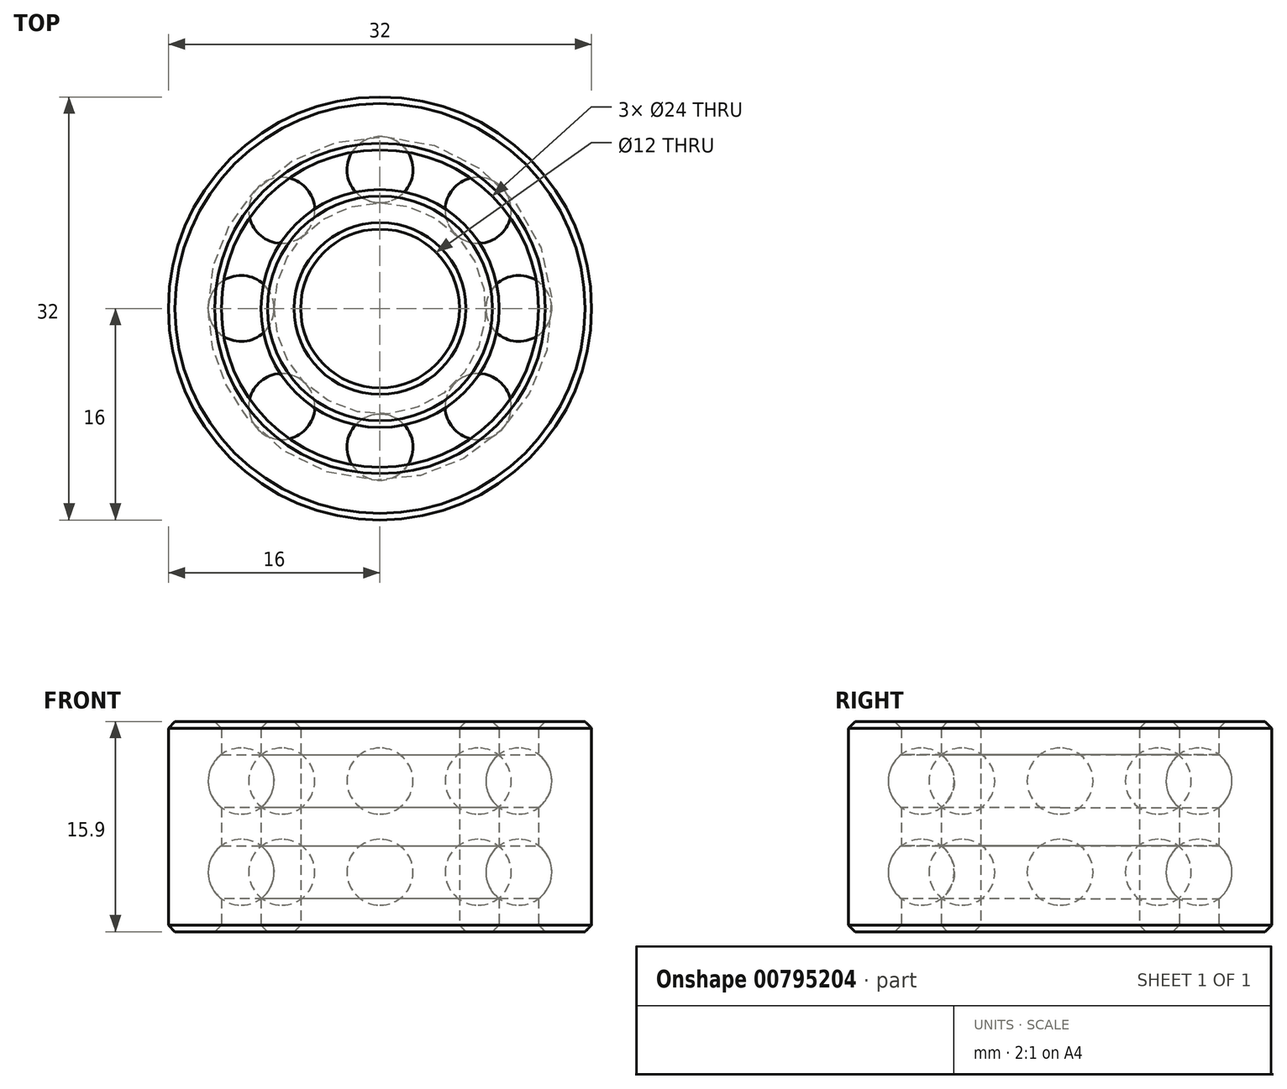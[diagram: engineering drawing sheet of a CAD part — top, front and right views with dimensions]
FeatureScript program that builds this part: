
annotation { "Feature Type Name" : "Feature", "Feature Type Description" : "" }
export const myFeature = defineFeature(function(context is Context, id is Id, definition is map)
    precondition{}
    {
        {
            var Q0;
            Q0=qCreatedBy(makeId("Top.planeOp"),FACE);
            var sketch = newSketch(context, id + "F0", { "sketchPlane" : qUnion([Q0])});
            skCircle(sketch, "E0", {"center": v(0, 0) * mm, "radius": 6 * mm});
            skCircle(sketch, "E1", {"center": v(0, 0) * mm, "radius": 16 * mm});
            skCircle(sketch, "E2", {"center": v(0, 0) * mm, "radius": 9 * mm});
            skCircle(sketch, "E3", {"center": v(0, 0) * mm, "radius": 12 * mm});
            skSolve(sketch);
        }
        {
            var Q0;
            Q0=makeQuery(id+"F0.imprint","IMPRINT",FACE,{"disambiguationData":[TD([[makeQuery(id+"F0.imprint","IMPRINT",EDGE,{"derivedFrom":sQuery(id+"F0.wireOp",EDGE,"E0")}),-1.0]])]});
            var Q1;
            Q1=makeQuery(id+"F0.imprint","IMPRINT",FACE,{"disambiguationData":[TD([[makeQuery(id+"F0.imprint","IMPRINT",EDGE,{"derivedFrom":sQuery(id+"F0.wireOp",EDGE,"E1")}),1.0]])]});
            extrude(context, id + "F1", {"entities" : qUnion([Q0, Q1]), "depth" : 15.9 * mm, "offsetDistance" : 25 * mm});
        }
        {
            var Q0;
            Q0=makeQuery(id+"F1.opExtrude","CAP_FACE",FACE,{"disambiguationData":[OSD([sQuery(id+"F0.wireOp",EDGE,"E1"),sQuery(id+"F0.wireOp",EDGE,"E3")])],"isStart":false});
            var Q1;
            Q1=makeQuery(id+"F1.opExtrude","CAP_FACE",FACE,{"disambiguationData":[OSD([sQuery(id+"F0.wireOp",EDGE,"E0"),sQuery(id+"F0.wireOp",EDGE,"E2")])],"isStart":false});
            var Q2;
            Q2=makeQuery(id+"F1.opExtrude","CAP_FACE",FACE,{"disambiguationData":[OSD([sQuery(id+"F0.wireOp",EDGE,"E1"),sQuery(id+"F0.wireOp",EDGE,"E3")])],"isStart":true});
            var Q3;
            Q3=makeQuery(id+"F1.opExtrude","CAP_FACE",FACE,{"disambiguationData":[OSD([sQuery(id+"F0.wireOp",EDGE,"E0"),sQuery(id+"F0.wireOp",EDGE,"E2")])],"isStart":true});
            chamfer(context, id + "F2", {"entities" : qUnion([Q0, Q1, Q2, Q3]), "width" : .5 * mm, "tangentPropagation" : true});
        }
        {
            var Q0;
            Q0=qCreatedBy(makeId("Front.planeOp"),FACE);
            var sketch = newSketch(context, id + "F3", { "sketchPlane" : qUnion([Q0])});
            skCircle(sketch, "E4", {"center": v(10.5, 11.4) * mm, "radius": 2.5 * mm});
            skCircle(sketch, "E5", {"center": v(10.5, 4.5) * mm, "radius": 2.5 * mm});
            skLineSegment(sketch, "E6", {"start": v(0, 17.94) * mm, "end": v(0, -2.67) * mm});
            skSolve(sketch);
        }
        {
            var Q0;
            Q0 = qSketchRegion(id + "F3", true);
            var Q1;
            Q1=sQuery(id+"F3.wireOp",EDGE,"E6");
            revolve(context, id + "F4", {"operationType" : NewBodyOperationType.REMOVE, "surfaceOperationType" : NewSurfaceOperationType.NEW, "entities" : qUnion([Q0]), "axis" : qUnion([Q1]), "revolveType" : RevolveType.FULL, "oppositeDirection" : true});
        }
        {
            var Q0;
            Q0=qCreatedBy(makeId("Front.planeOp"),FACE);
            var sketch = newSketch(context, id + "F5", { "sketchPlane" : qUnion([Q0])});
            skArc(sketch, "E7", {"start": v(10.5, 8.9) * mm, "mid": v(13, 11.4) * mm, "end": v(10.5, 13.9) * mm});
            skArc(sketch, "E8", {"start": v(10.5, 2) * mm, "mid": v(13, 4.5) * mm, "end": v(10.5, 7) * mm});
            skLineSegment(sketch, "E9", {"start": v(10.5, 11.4) * mm, "end": v(10.5, 13.9) * mm});
            skLineSegment(sketch, "E10", {"start": v(10.5, 11.4) * mm, "end": v(10.5, 8.9) * mm});
            skLineSegment(sketch, "E11", {"start": v(10.5, 4.5) * mm, "end": v(10.5, 7) * mm});
            skLineSegment(sketch, "E12", {"start": v(10.5, 4.5) * mm, "end": v(10.5, 2) * mm});
            skSolve(sketch);
        }
        {
            var Q0;
            Q0 = qSketchRegion(id + "F5", true);
            var Q1;
            Q1=sQuery(id+"F5.wireOp",EDGE,"E9");
            revolve(context, id + "F6", {"surfaceOperationType" : NewSurfaceOperationType.NEW, "entities" : qUnion([Q0]), "axis" : qUnion([Q1]), "revolveType" : RevolveType.FULL});
        }
        {
            var Q0;
            Q0=qCreatedBy(makeId("Front.planeOp"),FACE);
            var sketch = newSketch(context, id + "F7", { "sketchPlane" : qUnion([Q0])});
            skLineSegment(sketch, "E13", {"start": v(0, 47.8) * mm, "end": v(0, -43.73) * mm, "construction": true});
            skSolve(sketch);
        }
        {
            var Q0;
            Q0=makeQuery(id+"F6.opRevolve","SWEPT_BODY",BODY,{"disambiguationData":[OSD([sQuery(id+"F5.wireOp",EDGE,"E7"),sQuery(id+"F5.wireOp",EDGE,"E9"),sQuery(id+"F5.wireOp",EDGE,"E10")])]});
            var Q1;
            Q1=makeQuery(id+"F6.opRevolve","SWEPT_BODY",BODY,{"disambiguationData":[OSD([sQuery(id+"F5.wireOp",EDGE,"E8"),sQuery(id+"F5.wireOp",EDGE,"E11"),sQuery(id+"F5.wireOp",EDGE,"E12")])]});
            var Q2;
            Q2=sQuery(id+"F7.wireOp",EDGE,"E13");
            circularPattern(context, id + "F8", {"entities" : qUnion([Q0, Q1]), "axis" : qUnion([Q2]), "angle" : 360 * degree, "instanceCount" : 8, "equalSpace" : true});
        }
    });
